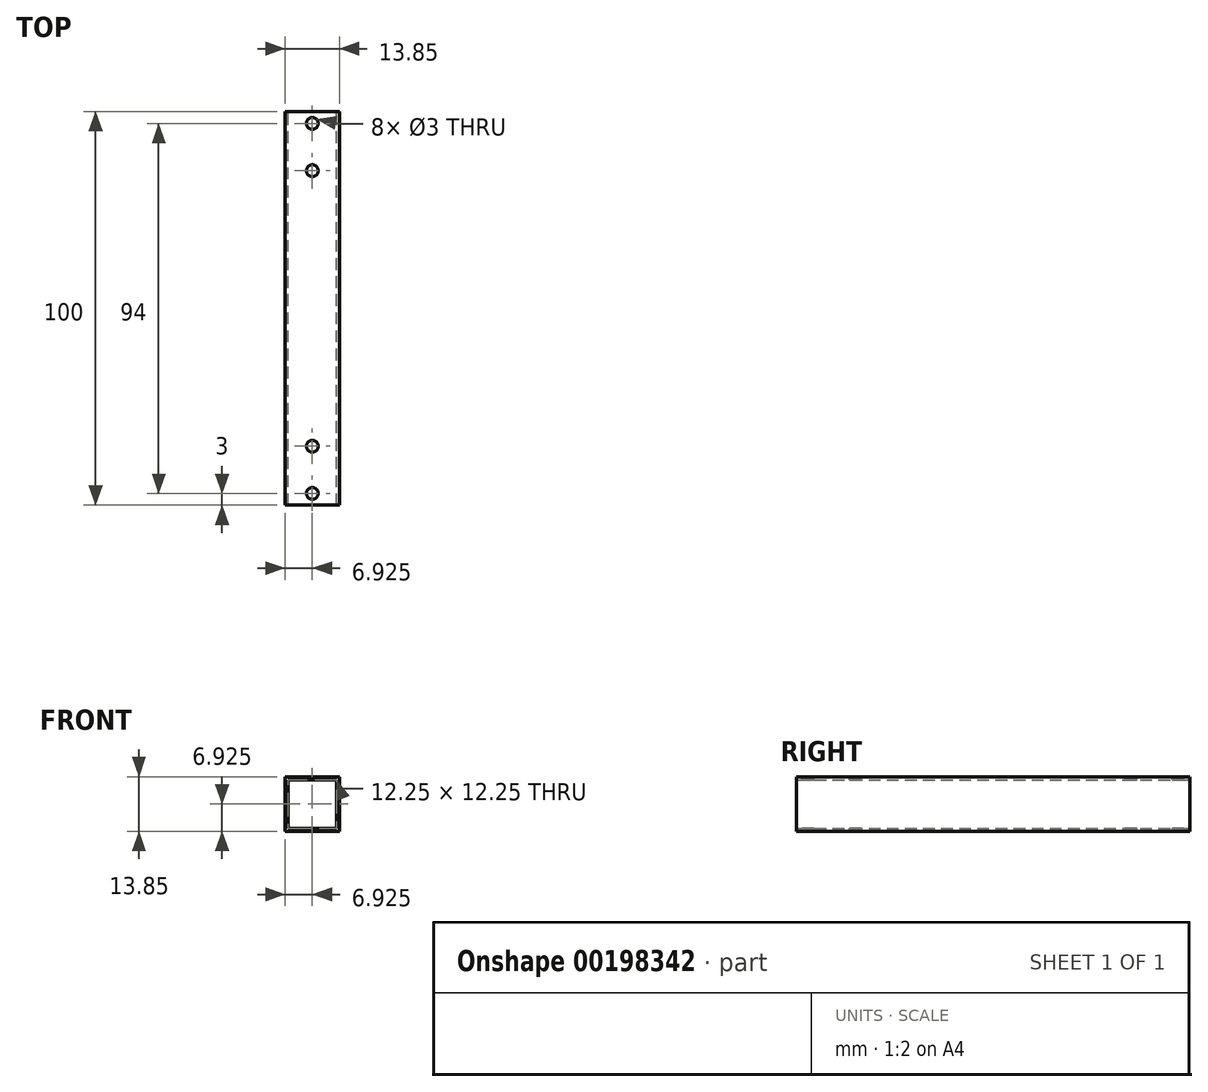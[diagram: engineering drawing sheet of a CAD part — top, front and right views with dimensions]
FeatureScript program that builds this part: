
annotation { "Feature Type Name" : "Feature", "Feature Type Description" : "" }
export const myFeature = defineFeature(function(context is Context, id is Id, definition is map)
    precondition{}
    {
        {
            var Q0;
            Q0=qCreatedBy(makeId("Front.planeOp"),FACE);
            var sketch = newSketch(context, id + "F0", { "sketchPlane" : qUnion([Q0])});
            skLineSegment(sketch, "E0.bottom", {"start": v(0, 0) * mm, "end": v(13.85, 0) * mm});
            skLineSegment(sketch, "E0.top", {"start": v(0, 13.85) * mm, "end": v(13.85, 13.85) * mm});
            skLineSegment(sketch, "E0.left", {"start": v(0, 0) * mm, "end": v(0, 13.85) * mm});
            skLineSegment(sketch, "E0.right", {"start": v(13.85, 0) * mm, "end": v(13.85, 13.85) * mm});
            skSolve(sketch);
        }
        {
            var Q0;
            Q0=makeQuery(id+"F0.imprint","IMPRINT",FACE,{"disambiguationData":[TD([[makeQuery(id+"F0.imprint","IMPRINT",EDGE,{"derivedFrom":sQuery(id+"F0.wireOp",EDGE,"E0.bottom")}),1.0]])]});
            extrude(context, id + "F1", {"entities" : qUnion([Q0]), "depth" : 100 * mm});
        }
        {
            var Q0;
            Q0=makeQuery(id+"F1.opExtrude","CAP_FACE",FACE,{"disambiguationData":[OSD([sQuery(id+"F0.wireOp",EDGE,"E0.bottom"),sQuery(id+"F0.wireOp",EDGE,"E0.top"),sQuery(id+"F0.wireOp",EDGE,"E0.left"),sQuery(id+"F0.wireOp",EDGE,"E0.right")])],"isStart":false});
            var Q1;
            Q1=makeQuery(id+"F1.opExtrude","CAP_FACE",FACE,{"disambiguationData":[OSD([sQuery(id+"F0.wireOp",EDGE,"E0.bottom"),sQuery(id+"F0.wireOp",EDGE,"E0.top"),sQuery(id+"F0.wireOp",EDGE,"E0.left"),sQuery(id+"F0.wireOp",EDGE,"E0.right")])],"isStart":true});
            shell(context, id + "F2", {"entities" : qUnion([Q0, Q1]), "thickness" : .8 * mm});
        }
        {
            var Q0;
            Q0=makeQuery(id+"F1.opExtrude","SWEPT_FACE",FACE,{"disambiguationData":[OSD([sQuery(id+"F0.wireOp",EDGE,"E0.top")])]});
            var sketch = newSketch(context, id + "F3", { "sketchPlane" : qUnion([Q0])});
            skCircle(sketch, "E1", {"center": v(6.93, -97) * mm, "radius": 1.5 * mm});
            skCircle(sketch, "E2", {"center": v(6.92, -85) * mm, "radius": 1.5 * mm});
            skCircle(sketch, "E3", {"center": v(6.92, -15) * mm, "radius": 1.5 * mm});
            skCircle(sketch, "E4", {"center": v(6.92, -3) * mm, "radius": 1.5 * mm});
            skSolve(sketch);
        }
        {
            var Q0;
            Q0=makeQuery(id+"F3.imprint","IMPRINT",FACE,{"disambiguationData":[TD([[makeQuery(id+"F3.imprint","IMPRINT",EDGE,{"derivedFrom":sQuery(id+"F3.wireOp",EDGE,"E1")}),1.0]])]});
            var Q1;
            Q1=makeQuery(id+"F3.imprint","IMPRINT",FACE,{"disambiguationData":[TD([[makeQuery(id+"F3.imprint","IMPRINT",EDGE,{"derivedFrom":sQuery(id+"F3.wireOp",EDGE,"E2")}),1.0]])]});
            var Q2;
            Q2=makeQuery(id+"F3.imprint","IMPRINT",FACE,{"disambiguationData":[TD([[makeQuery(id+"F3.imprint","IMPRINT",EDGE,{"derivedFrom":sQuery(id+"F3.wireOp",EDGE,"E3")}),1.0]])]});
            var Q3;
            Q3=makeQuery(id+"F3.imprint","IMPRINT",FACE,{"disambiguationData":[TD([[makeQuery(id+"F3.imprint","IMPRINT",EDGE,{"derivedFrom":sQuery(id+"F3.wireOp",EDGE,"E4")}),1.0]])]});
            extrude(context, id + "F4", {"entities" : qUnion([Q0, Q1, Q2, Q3]), "operationType" : NewBodyOperationType.REMOVE, "oppositeDirection" : true, "depth" : 25 * mm});
        }
    });
